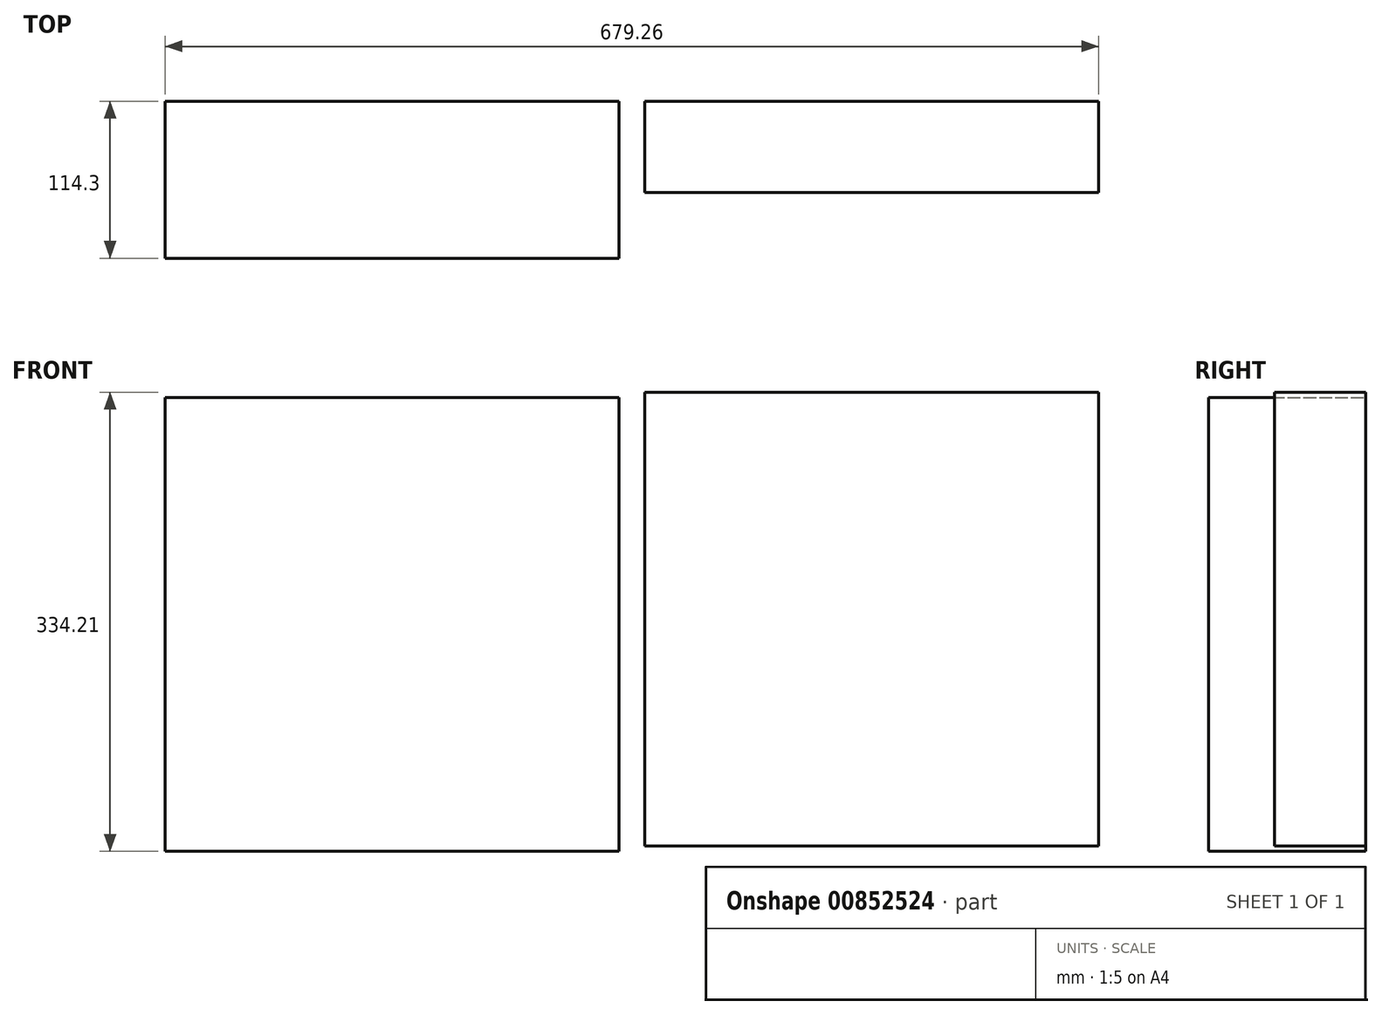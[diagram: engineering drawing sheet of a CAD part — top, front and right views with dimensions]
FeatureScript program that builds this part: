
annotation { "Feature Type Name" : "Feature", "Feature Type Description" : "" }
export const myFeature = defineFeature(function(context is Context, id is Id, definition is map)
    precondition{}
    {
        {
            var Q0;
            Q0=qCreatedBy(makeId("Front.planeOp"),FACE);
            var sketch = newSketch(context, id + "F0", { "sketchPlane" : qUnion([Q0])});
            skPoint(sketch, "E0.middle", {"position": v(0, 0) * mm});
            skLineSegment(sketch, "E1.bottom", {"start": v(165.1, -165.1) * mm, "end": v(-165.1, -165.1) * mm});
            skLineSegment(sketch, "E1.top", {"start": v(165.1, 165.1) * mm, "end": v(-165.1, 165.1) * mm});
            skLineSegment(sketch, "E1.left", {"start": v(165.1, -165.1) * mm, "end": v(165.1, 165.1) * mm});
            skLineSegment(sketch, "E1.right", {"start": v(-165.1, -165.1) * mm, "end": v(-165.1, 165.1) * mm});
            skSolve(sketch);
        }
        {
            var Q0;
            Q0 = qSketchRegion(id + "F0", true);
            extrude(context, id + "F1", {"entities" : qUnion([Q0]), "depth" : 114.3 * mm, "offsetDistance" : 25.4 * mm});
        }
        {
            var Q0;
            Q0=qCreatedBy(makeId("Front.planeOp"),FACE);
            var sketch = newSketch(context, id + "F2", { "sketchPlane" : qUnion([Q0])});
            skLineSegment(sketch, "E2.bottom", {"start": v(183.96, 169.1) * mm, "end": v(514.16, 169.1) * mm});
            skLineSegment(sketch, "E2.top", {"start": v(183.96, -161.1) * mm, "end": v(514.16, -161.1) * mm});
            skLineSegment(sketch, "E2.left", {"start": v(183.96, 169.1) * mm, "end": v(183.96, -161.1) * mm});
            skLineSegment(sketch, "E2.right", {"start": v(514.16, 169.1) * mm, "end": v(514.16, -161.1) * mm});
            skSolve(sketch);
        }
        {
            var Q0;
            Q0 = qSketchRegion(id + "F2", true);
            extrude(context, id + "F3", {"entities" : qUnion([Q0]), "depth" : 66.55 * mm, "offsetDistance" : 25.4 * mm});
        }
    });
